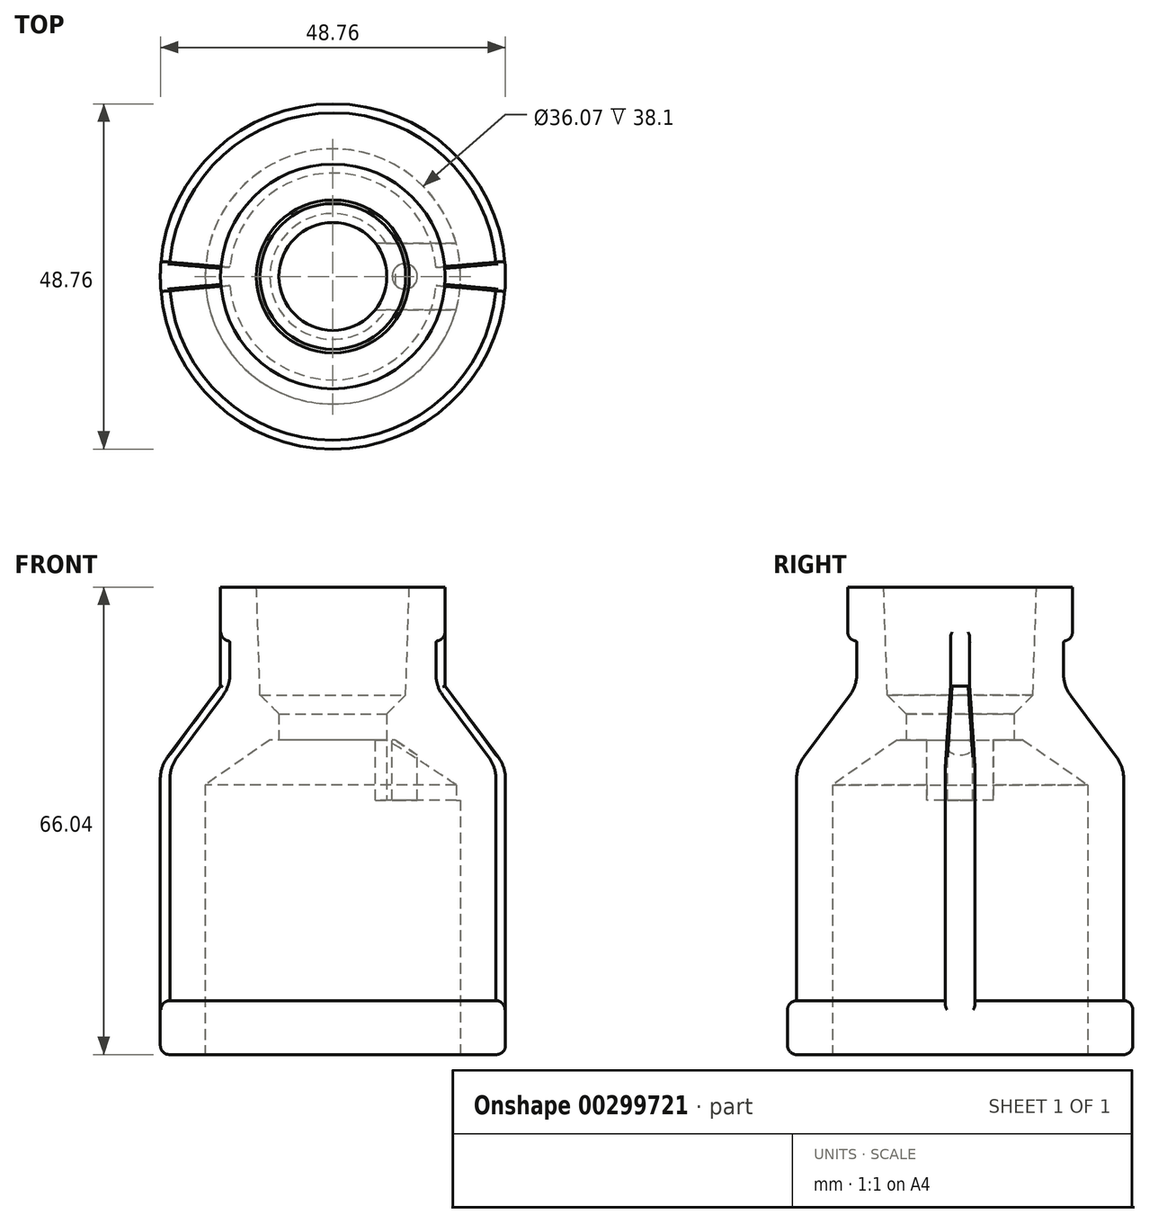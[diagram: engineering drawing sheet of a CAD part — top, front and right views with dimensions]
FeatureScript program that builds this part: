
annotation { "Feature Type Name" : "Feature", "Feature Type Description" : "" }
export const myFeature = defineFeature(function(context is Context, id is Id, definition is map)
    precondition{}
    {
        {
            var Q0;
            Q0=qCreatedBy(makeId("Front.planeOp"),FACE);
            var sketch = newSketch(context, id + "F0", { "sketchPlane" : qUnion([Q0])});
            skLineSegment(sketch, "E0", {"start": v(0, 1.67) * mm, "end": v(0, 16.9) * mm});
            skLineSegment(sketch, "E1", {"start": v(0, 16.9) * mm, "end": v(10.8, 16.9) * mm});
            skLineSegment(sketch, "E2", {"start": v(10.8, 16.9) * mm, "end": v(15.88, 16.9) * mm});
            skLineSegment(sketch, "E3", {"start": v(15.88, 16.9) * mm, "end": v(15.88, 9.29) * mm});
            skLineSegment(sketch, "E4", {"start": v(15.88, 9.29) * mm, "end": v(14.6, 9.29) * mm});
            skLineSegment(sketch, "E5", {"start": v(0, 1.67) * mm, "end": v(10.29, 1.67) * mm});
            skLineSegment(sketch, "E6", {"start": v(10.29, 1.67) * mm, "end": v(10.8, 16.9) * mm});
            skLineSegment(sketch, "E7", {"start": v(0, 1.67) * mm, "end": v(0, -4.68) * mm});
            skLineSegment(sketch, "E8", {"start": v(0, -4.68) * mm, "end": v(8.9, -4.68) * mm});
            skLineSegment(sketch, "E9", {"start": v(0, -4.68) * mm, "end": v(0, -11.03) * mm});
            skLineSegment(sketch, "E10", {"start": v(0, -11.03) * mm, "end": v(18.03, -11.03) * mm});
            skLineSegment(sketch, "E11", {"start": v(18.03, -11.03) * mm, "end": v(18.03, -49.13) * mm});
            skLineSegment(sketch, "E12", {"start": v(8.89, -4.68) * mm, "end": v(18.03, -11.03) * mm});
            skLineSegment(sketch, "E13", {"start": v(18.03, -49.13) * mm, "end": v(24.38, -49.13) * mm});
            skLineSegment(sketch, "E14", {"start": v(24.38, -49.13) * mm, "end": v(24.38, -41.51) * mm});
            skLineSegment(sketch, "E15", {"start": v(24.38, -41.51) * mm, "end": v(23.11, -41.51) * mm});
            skLineSegment(sketch, "E16", {"start": v(23.11, -41.51) * mm, "end": v(23.11, -8.5) * mm});
            skLineSegment(sketch, "E17", {"start": v(14.6, 9.29) * mm, "end": v(14.6, 2.94) * mm});
            skLineSegment(sketch, "E18", {"start": v(14.6, 2.94) * mm, "end": v(23.11, -8.5) * mm});
            skLineSegment(sketch, "E19", {"start": v(0, 1.67) * mm, "end": v(0, -8.62) * mm});
            skLineSegment(sketch, "E20", {"start": v(0, -4.68) * mm, "end": v(7.62, -4.68) * mm});
            skLineSegment(sketch, "E21", {"start": v(7.62, -4.68) * mm, "end": v(7.62, -1) * mm});
            skLineSegment(sketch, "E22", {"start": v(10.29, 1.67) * mm, "end": v(7.62, -1) * mm});
            skLineSegment(sketch, "E23", {"start": v(15.88, 9.29) * mm, "end": v(15.88, 2.94) * mm});
            skLineSegment(sketch, "E24", {"start": v(15.88, 2.94) * mm, "end": v(24.38, -8.5) * mm});
            skLineSegment(sketch, "E25", {"start": v(24.38, -8.5) * mm, "end": v(24.38, -41.51) * mm});
            skLineSegment(sketch, "E26", {"start": v(14.6, 9.29) * mm, "end": v(14.6, 12.15) * mm});
            skLineSegment(sketch, "E27", {"start": v(14.6, 12.15) * mm, "end": v(15.88, 12.1) * mm});
            skLineSegment(sketch, "E28", {"start": v(24.38, -41.51) * mm, "end": v(24.38, -43.7) * mm});
            skLineSegment(sketch, "E29", {"start": v(24.38, -43.7) * mm, "end": v(23.11, -43.7) * mm});
            skLineSegment(sketch, "E30", {"start": v(23.11, -43.7) * mm, "end": v(23.11, -41.51) * mm});
            skLineSegment(sketch, "E31.MirrorCS", {"start": v(-24.38, -8.5) * mm, "end": v(-24.38, -41.51) * mm});
            skLineSegment(sketch, "E32.MirrorCS", {"start": v(-15.87, 2.94) * mm, "end": v(-24.38, -8.5) * mm});
            skLineSegment(sketch, "E33.MirrorCS", {"start": v(-14.6, 2.94) * mm, "end": v(-23.11, -8.5) * mm});
            skLineSegment(sketch, "E34.MirrorCS", {"start": v(-23.11, -41.51) * mm, "end": v(-23.11, -8.5) * mm});
            skLineSegment(sketch, "E35.MirrorCS", {"start": v(-24.38, -41.51) * mm, "end": v(-24.38, -43.7) * mm});
            skLineSegment(sketch, "E36.MirrorCS", {"start": v(-23.11, -43.7) * mm, "end": v(-23.11, -41.51) * mm});
            skLineSegment(sketch, "E37.MirrorCS", {"start": v(-24.38, -43.7) * mm, "end": v(-23.11, -43.7) * mm});
            skLineSegment(sketch, "E38.MirrorCS", {"start": v(-14.6, 12.15) * mm, "end": v(-15.88, 12.1) * mm});
            skLineSegment(sketch, "E39.MirrorCS", {"start": v(-14.6, 9.29) * mm, "end": v(-14.6, 12.15) * mm});
            skLineSegment(sketch, "E40.MirrorCS", {"start": v(-15.88, 16.9) * mm, "end": v(-15.88, 9.29) * mm});
            skLineSegment(sketch, "E41.MirrorCS", {"start": v(-14.6, 9.29) * mm, "end": v(-14.6, 2.94) * mm});
            skLineSegment(sketch, "E42.MirrorCS", {"start": v(-15.88, 9.29) * mm, "end": v(-15.88, 2.94) * mm});
            skSolve(sketch);
        }
        {
            var Q0;
            Q0=makeQuery(id+"F0.imprint","IMPRINT",FACE,{"disambiguationData":[TD([[makeQuery(id+"F0.imprint","IMPRINT",EDGE,{"derivedFrom":sQuery(id+"F0.wireOp",EDGE,"E2")}),-1.0]])]});
            var Q1;
            Q1=makeQuery(id+"F0.imprint","IMPRINT",FACE,{"disambiguationData":[TD([[makeQuery(id+"F0.imprint","IMPRINT",EDGE,{"derivedFrom":sQuery(id+"F0.wireOp",EDGE,"E15")}),1.0]])]});
            var Q2;
            {var subQ0=sQuery(id+"F0.wireOp",EDGE,"E4");Q2=makeQuery(id+"F0.imprint","IMPRINT",FACE,{"disambiguationData":[TD([[makeQuery(id+"F0.imprint","IMPRINT",EDGE,{"derivedFrom":subQ0}),-1.0]])]});}
            var Q3;
            Q3=sQuery(id+"F0.wireOp",EDGE,"E0");
            revolve(context, id + "F1", {"entities" : qUnion([Q0, Q1, Q2]), "axis" : qUnion([Q3]), "revolveType" : RevolveType.FULL});
        }
        {
            var Q0;
            Q0=makeQuery(id+"F1.opRevolve","SWEPT_EDGE",EDGE,{"disambiguationData":[OSD([sQuery(id+"F0.wireOp",EDGE,"E3"),sQuery(id+"F0.wireOp",EDGE,"E4")])]});
            var Q1;
            Q1=makeQuery(id+"F1.opRevolve","SWEPT_EDGE",EDGE,{"disambiguationData":[OSD([sQuery(id+"F0.wireOp",EDGE,"E14"),sQuery(id+"F0.wireOp",EDGE,"E15")])]});
            var Q2;
            Q2=makeQuery(id+"F1.opRevolve","SWEPT_EDGE",EDGE,{"disambiguationData":[OSD([sQuery(id+"F0.wireOp",EDGE,"E13"),sQuery(id+"F0.wireOp",EDGE,"E14")])]});
            fillet(context, id + "F2", {"entities" : qUnion([Q0, Q1, Q2]), "radius" : 1.27 * mm, "tangentPropagation" : true, "allowEdgeOverflow" : false});
        }
        {
            var Q0;
            Q0=makeQuery(id+"F1.opRevolve","SWEPT_EDGE",EDGE,{"disambiguationData":[OSD([sQuery(id+"F0.wireOp",EDGE,"E17"),sQuery(id+"F0.wireOp",EDGE,"E18")])]});
            var Q1;
            Q1=makeQuery(id+"F1.opRevolve","SWEPT_EDGE",EDGE,{"disambiguationData":[OSD([sQuery(id+"F0.wireOp",EDGE,"E16"),sQuery(id+"F0.wireOp",EDGE,"E18")])]});
            fillet(context, id + "F3", {"entities" : qUnion([Q0, Q1]), "radius" : 5.08 * mm, "tangentPropagation" : true, "allowEdgeOverflow" : false});
        }
        {
            var Q0;
            Q0=makeQuery(id+"F0.imprint","IMPRINT",FACE,{"disambiguationData":[TD([[makeQuery(id+"F0.imprint","IMPRINT",EDGE,{"derivedFrom":sQuery(id+"F0.wireOp",EDGE,"E4")}),1.0]])]});
            var Q1;
            Q1=makeQuery(id+"F0.imprint","IMPRINT",FACE,{"disambiguationData":[TD([[makeQuery(id+"F0.imprint","IMPRINT",EDGE,{"derivedFrom":sQuery(id+"F0.wireOp",EDGE,"E15")}),1.0]])]});
            var Q2;
            {var subQ0=sQuery(id+"F0.wireOp",EDGE,"E4");Q2=makeQuery(id+"F0.imprint","IMPRINT",FACE,{"disambiguationData":[TD([[makeQuery(id+"F0.imprint","IMPRINT",EDGE,{"derivedFrom":subQ0}),-1.0]])]});}
            var Q3;
            Q3=sQuery(id+"F0.wireOp",EDGE,"E0");
            revolve(context, id + "F4", {"operationType" : NewBodyOperationType.ADD, "entities" : qUnion([Q0, Q1, Q2]), "axis" : qUnion([Q3]), "revolveType" : RevolveType.SYMMETRIC, "angle" : 10 * degree});
        }
        {
            var Q0;
            Q0=makeQuery(id+"F4.opRevolve","SWEPT_EDGE",EDGE,{"disambiguationData":[OSD([sQuery(id+"F0.wireOp",EDGE,"E16"),sQuery(id+"F0.wireOp",EDGE,"E18")])]});
            var Q1;
            Q1=makeQuery(id+"F4.opRevolve","SWEPT_EDGE",EDGE,{"disambiguationData":[OSD([sQuery(id+"F0.wireOp",EDGE,"E24"),sQuery(id+"F0.wireOp",EDGE,"E25")])]});
            fillet(context, id + "F5", {"entities" : qUnion([Q0, Q1]), "radius" : 5.08 * mm, "tangentPropagation" : true, "allowEdgeOverflow" : false});
        }
        {
            var Q0;
            Q0=makeQuery(id+"F0.imprint","IMPRINT",FACE,{"disambiguationData":[TD([[makeQuery(id+"F0.imprint","IMPRINT",EDGE,{"derivedFrom":sQuery(id+"F0.wireOp",EDGE,"E31.MirrorCS")}),1.0]])]});
            var Q1;
            Q1=sQuery(id+"F0.wireOp",EDGE,"E0");
            revolve(context, id + "F6", {"operationType" : NewBodyOperationType.ADD, "entities" : qUnion([Q0]), "axis" : qUnion([Q1]), "revolveType" : RevolveType.SYMMETRIC, "angle" : 10 * degree});
        }
        {
            var Q0;
            Q0=makeQuery(id+"F6.opRevolve","SWEPT_EDGE",EDGE,{"disambiguationData":[OSD([sQuery(id+"F0.wireOp",EDGE,"E33.MirrorCS"),sQuery(id+"F0.wireOp",EDGE,"E34.MirrorCS")])]});
            var Q1;
            Q1=makeQuery(id+"F6.opRevolve","SWEPT_EDGE",EDGE,{"disambiguationData":[OSD([sQuery(id+"F0.wireOp",EDGE,"E31.MirrorCS"),sQuery(id+"F0.wireOp",EDGE,"E32.MirrorCS")])]});
            fillet(context, id + "F7", {"entities" : qUnion([Q0, Q1]), "radius" : 5.08 * mm, "tangentPropagation" : true, "allowEdgeOverflow" : false});
        }
        {
            var Q0;
            Q0=makeQuery(id+"F4.opRevolve","CAP_EDGE",EDGE,{"disambiguationData":[OSD([sQuery(id+"F0.wireOp",EDGE,"E24")])],"isStart":false});
            var Q1;
            Q1=makeQuery(id+"F4.opRevolve","CAP_EDGE",EDGE,{"disambiguationData":[OSD([sQuery(id+"F0.wireOp",EDGE,"E24")])],"isStart":true});
            var Q2;
            Q2=makeQuery(id+"F4.opRevolve","CAP_EDGE",EDGE,{"disambiguationData":[OSD([sQuery(id+"F0.wireOp",EDGE,"E3"),sQuery(id+"F0.wireOp",EDGE,"E23")])],"isStart":false});
            var Q3;
            Q3=makeQuery(id+"F4.opRevolve","CAP_EDGE",EDGE,{"disambiguationData":[OSD([sQuery(id+"F0.wireOp",EDGE,"E3"),sQuery(id+"F0.wireOp",EDGE,"E23")])],"isStart":true});
            var Q4;
            Q4=makeQuery(id+"F6.opRevolve","CAP_EDGE",EDGE,{"disambiguationData":[OSD([sQuery(id+"F0.wireOp",EDGE,"E32.MirrorCS")])],"isStart":true});
            var Q5;
            Q5=makeQuery(id+"F6.opRevolve","CAP_EDGE",EDGE,{"disambiguationData":[OSD([sQuery(id+"F0.wireOp",EDGE,"E40.MirrorCS"),sQuery(id+"F0.wireOp",EDGE,"E42.MirrorCS")])],"isStart":true});
            var Q6;
            Q6=makeQuery(id+"F6.opRevolve","CAP_EDGE",EDGE,{"disambiguationData":[OSD([sQuery(id+"F0.wireOp",EDGE,"E40.MirrorCS"),sQuery(id+"F0.wireOp",EDGE,"E42.MirrorCS")])],"isStart":false});
            var Q7;
            Q7=makeQuery(id+"F6.opRevolve","CAP_EDGE",EDGE,{"disambiguationData":[OSD([sQuery(id+"F0.wireOp",EDGE,"E32.MirrorCS")])],"isStart":false});
            var Q8;
            Q8=makeQuery(id+"F6.opRevolve","CAP_EDGE",EDGE,{"disambiguationData":[OSD([sQuery(id+"F0.wireOp",EDGE,"E39.MirrorCS"),sQuery(id+"F0.wireOp",EDGE,"E41.MirrorCS")])],"isStart":true});
            var Q9;
            Q9=makeQuery(id+"F6.opRevolve","CAP_EDGE",EDGE,{"disambiguationData":[OSD([sQuery(id+"F0.wireOp",EDGE,"E39.MirrorCS"),sQuery(id+"F0.wireOp",EDGE,"E41.MirrorCS")])],"isStart":false});
            var Q10;
            {var subQ0=sQuery(id+"F0.wireOp",EDGE,"E17");var subQ1=makeQuery(id+"F1.opRevolve","SWEPT_FACE",FACE,{"disambiguationData":[OSD([subQ0])]});var subQ2=sQuery(id+"F0.wireOp",EDGE,"E23");var subQ3=sQuery(id+"F0.wireOp",EDGE,"E4");var subQ4=sQuery(id+"F0.wireOp",EDGE,"E3");Q10=makeQuery(id+"F6.boolean.opBoolean","SPLIT",EDGE,{"disambiguationData":[TD([makeQuery(id+"F4.opRevolve","CAP_FACE",FACE,{"disambiguationData":[OSD([subQ4,sQuery(id+"F0.wireOp",EDGE,"E16"),subQ0,sQuery(id+"F0.wireOp",EDGE,"E18"),subQ2,sQuery(id+"F0.wireOp",EDGE,"E24"),sQuery(id+"F0.wireOp",EDGE,"E25"),sQuery(id+"F0.wireOp",EDGE,"E26"),sQuery(id+"F0.wireOp",EDGE,"E27"),sQuery(id+"F0.wireOp",EDGE,"E28"),sQuery(id+"F0.wireOp",EDGE,"E29"),sQuery(id+"F0.wireOp",EDGE,"E30")])],"isStart":true})])],"derivedFrom":makeQuery(id+"F2.opFillet","BLEND_EDGE",EDGE,{"blendedFrom":[makeQuery(id+"F1.opRevolve","SWEPT_EDGE",EDGE,{"disambiguationData":[OSD([subQ4,subQ3,subQ2])]}),subQ1],"blendedInto":[subQ1]})});}
            var Q11;
            {var subQ0=sQuery(id+"F0.wireOp",EDGE,"E17");var subQ1=makeQuery(id+"F1.opRevolve","SWEPT_FACE",FACE,{"disambiguationData":[OSD([subQ0])]});var subQ2=sQuery(id+"F0.wireOp",EDGE,"E23");var subQ3=sQuery(id+"F0.wireOp",EDGE,"E4");var subQ4=sQuery(id+"F0.wireOp",EDGE,"E3");Q11=makeQuery(id+"F6.boolean.opBoolean","SPLIT",EDGE,{"disambiguationData":[TD([makeQuery(id+"F4.opRevolve","CAP_FACE",FACE,{"disambiguationData":[OSD([subQ4,sQuery(id+"F0.wireOp",EDGE,"E16"),subQ0,sQuery(id+"F0.wireOp",EDGE,"E18"),subQ2,sQuery(id+"F0.wireOp",EDGE,"E24"),sQuery(id+"F0.wireOp",EDGE,"E25"),sQuery(id+"F0.wireOp",EDGE,"E26"),sQuery(id+"F0.wireOp",EDGE,"E27"),sQuery(id+"F0.wireOp",EDGE,"E28"),sQuery(id+"F0.wireOp",EDGE,"E29"),sQuery(id+"F0.wireOp",EDGE,"E30")])],"isStart":false})])],"derivedFrom":makeQuery(id+"F2.opFillet","BLEND_EDGE",EDGE,{"blendedFrom":[makeQuery(id+"F1.opRevolve","SWEPT_EDGE",EDGE,{"disambiguationData":[OSD([subQ4,subQ3,subQ2])]}),subQ1],"blendedInto":[subQ1]})});}
            var Q12;
            Q12=makeQuery(id+"F4.opRevolve","CAP_EDGE",EDGE,{"disambiguationData":[OSD([sQuery(id+"F0.wireOp",EDGE,"E17"),sQuery(id+"F0.wireOp",EDGE,"E26")])],"isStart":false});
            var Q13;
            Q13=makeQuery(id+"F4.opRevolve","CAP_EDGE",EDGE,{"disambiguationData":[OSD([sQuery(id+"F0.wireOp",EDGE,"E17"),sQuery(id+"F0.wireOp",EDGE,"E26")])],"isStart":true});
            var Q14;
            {var subQ0=sQuery(id+"F0.wireOp",EDGE,"E15");var subQ1=sQuery(id+"F0.wireOp",EDGE,"E16");var subQ2=sQuery(id+"F0.wireOp",EDGE,"E30");Q14=makeQuery(id+"F6.boolean.opBoolean","SPLIT",EDGE,{"disambiguationData":[TD([makeQuery(id+"F4.opRevolve","CAP_FACE",FACE,{"disambiguationData":[OSD([sQuery(id+"F0.wireOp",EDGE,"E3"),subQ1,sQuery(id+"F0.wireOp",EDGE,"E17"),sQuery(id+"F0.wireOp",EDGE,"E18"),sQuery(id+"F0.wireOp",EDGE,"E23"),sQuery(id+"F0.wireOp",EDGE,"E24"),sQuery(id+"F0.wireOp",EDGE,"E25"),sQuery(id+"F0.wireOp",EDGE,"E26"),sQuery(id+"F0.wireOp",EDGE,"E27"),sQuery(id+"F0.wireOp",EDGE,"E28"),sQuery(id+"F0.wireOp",EDGE,"E29"),subQ2])],"isStart":true})])],"derivedFrom":makeQuery(id+"F1.opRevolve","SWEPT_EDGE",EDGE,{"disambiguationData":[OSD([subQ0,subQ1,subQ2])]})});}
            var Q15;
            {var subQ0=sQuery(id+"F0.wireOp",EDGE,"E28");var subQ1=sQuery(id+"F0.wireOp",EDGE,"E25");var subQ2=sQuery(id+"F0.wireOp",EDGE,"E15");Q15=makeQuery(id+"F6.boolean.opBoolean","SPLIT",EDGE,{"disambiguationData":[TD([makeQuery(id+"F4.opRevolve","CAP_FACE",FACE,{"disambiguationData":[OSD([sQuery(id+"F0.wireOp",EDGE,"E3"),sQuery(id+"F0.wireOp",EDGE,"E16"),sQuery(id+"F0.wireOp",EDGE,"E17"),sQuery(id+"F0.wireOp",EDGE,"E18"),sQuery(id+"F0.wireOp",EDGE,"E23"),sQuery(id+"F0.wireOp",EDGE,"E24"),subQ1,sQuery(id+"F0.wireOp",EDGE,"E26"),sQuery(id+"F0.wireOp",EDGE,"E27"),subQ0,sQuery(id+"F0.wireOp",EDGE,"E29"),sQuery(id+"F0.wireOp",EDGE,"E30")])],"isStart":true})])],"derivedFrom":makeQuery(id+"F1.opRevolve","SWEPT_EDGE",EDGE,{"disambiguationData":[OSD([subQ2,subQ1,subQ0])]})});}
            var Q16;
            {var subQ0=sQuery(id+"F0.wireOp",EDGE,"E15");var subQ1=sQuery(id+"F0.wireOp",EDGE,"E30");var subQ2=sQuery(id+"F0.wireOp",EDGE,"E16");Q16=makeQuery(id+"F6.boolean.opBoolean","SPLIT",EDGE,{"disambiguationData":[TD([makeQuery(id+"F4.opRevolve","CAP_FACE",FACE,{"disambiguationData":[OSD([sQuery(id+"F0.wireOp",EDGE,"E3"),subQ2,sQuery(id+"F0.wireOp",EDGE,"E17"),sQuery(id+"F0.wireOp",EDGE,"E18"),sQuery(id+"F0.wireOp",EDGE,"E23"),sQuery(id+"F0.wireOp",EDGE,"E24"),sQuery(id+"F0.wireOp",EDGE,"E25"),sQuery(id+"F0.wireOp",EDGE,"E26"),sQuery(id+"F0.wireOp",EDGE,"E27"),sQuery(id+"F0.wireOp",EDGE,"E28"),sQuery(id+"F0.wireOp",EDGE,"E29"),subQ1])],"isStart":false})])],"derivedFrom":makeQuery(id+"F1.opRevolve","SWEPT_EDGE",EDGE,{"disambiguationData":[OSD([subQ0,subQ2,subQ1])]})});}
            var Q17;
            {var subQ0=sQuery(id+"F0.wireOp",EDGE,"E28");var subQ1=sQuery(id+"F0.wireOp",EDGE,"E25");var subQ4=sQuery(id+"F0.wireOp",EDGE,"E15");Q17=makeQuery(id+"F6.boolean.opBoolean","SPLIT",EDGE,{"disambiguationData":[TD([makeQuery(id+"F4.opRevolve","CAP_FACE",FACE,{"disambiguationData":[OSD([sQuery(id+"F0.wireOp",EDGE,"E3"),sQuery(id+"F0.wireOp",EDGE,"E16"),sQuery(id+"F0.wireOp",EDGE,"E17"),sQuery(id+"F0.wireOp",EDGE,"E18"),sQuery(id+"F0.wireOp",EDGE,"E23"),sQuery(id+"F0.wireOp",EDGE,"E24"),subQ1,sQuery(id+"F0.wireOp",EDGE,"E26"),sQuery(id+"F0.wireOp",EDGE,"E27"),subQ0,sQuery(id+"F0.wireOp",EDGE,"E29"),sQuery(id+"F0.wireOp",EDGE,"E30")])],"isStart":false})])],"derivedFrom":makeQuery(id+"F1.opRevolve","SWEPT_EDGE",EDGE,{"disambiguationData":[OSD([subQ4,subQ1,subQ0])]})});}
            fillet(context, id + "F8", {"entities" : qUnion([Q0, Q1, Q2, Q3, Q4, Q5, Q6, Q7, Q8, Q9, Q10, Q11, Q12, Q13, Q14, Q15, Q16, Q17]), "radius" : 0.25 * mm, "tangentPropagation" : true, "allowEdgeOverflow" : false});
        }
        {
            var Q0;
            Q0=makeQuery(id+"F1.opRevolve","SWEPT_FACE",FACE,{"disambiguationData":[OSD([sQuery(id+"F0.wireOp",EDGE,"E8")])]});
            var sketch = newSketch(context, id + "F9", { "sketchPlane" : qUnion([Q0])});
            skLineSegment(sketch, "E43", {"start": v(0, 0) * mm, "end": v(18.03, 0) * mm});
            skLineSegment(sketch, "E44", {"start": v(18.03, 0) * mm, "end": v(18.03, -4.7) * mm});
            skLineSegment(sketch, "E45", {"start": v(18.03, -4.7) * mm, "end": v(5.08, -4.7) * mm});
            skLineSegment(sketch, "E46", {"start": v(5.08, -4.7) * mm, "end": v(5.08, 4.7) * mm});
            skLineSegment(sketch, "E47", {"start": v(5.08, 4.7) * mm, "end": v(18.03, 4.7) * mm});
            skLineSegment(sketch, "E48", {"start": v(18.03, 4.7) * mm, "end": v(18.03, 0) * mm});
            skLineSegment(sketch, "E49", {"start": v(18.03, 0) * mm, "end": v(10.16, 0) * mm});
            skCircle(sketch, "E50", {"center": v(10.16, 0) * mm, "radius": 1.78 * mm});
            skCircle(sketch, "E51", {"center": v(0, 0) * mm, "radius": 7.62 * mm});
            skSolve(sketch);
        }
        {
            var Q0;
            {var subQ0=sQuery(id+"F9.wireOp",EDGE,"E51");var subQ1=sQuery(id+"F9.wireOp",EDGE,"E43");var subQ2=makeQuery(id+"F9.imprint","INTERSECT",VERTEX,{"derivedFrom":[subQ1,subQ0]});Q0=makeQuery(id+"F9.imprint","IMPRINT",FACE,{"disambiguationData":[TD([[makeQuery(id+"F9.imprint","IMPRINT",EDGE,{"disambiguationData":[TD([[subQ2,-1.0]])],"derivedFrom":subQ1}),1.0]])]});}
            var Q1;
            {var subQ0=sQuery(id+"F9.wireOp",EDGE,"E51");var subQ1=sQuery(id+"F9.wireOp",EDGE,"E43");var subQ2=makeQuery(id+"F9.imprint","INTERSECT",VERTEX,{"derivedFrom":[subQ1,subQ0]});Q1=makeQuery(id+"F9.imprint","IMPRINT",FACE,{"disambiguationData":[TD([[makeQuery(id+"F9.imprint","IMPRINT",EDGE,{"disambiguationData":[TD([[subQ2,-1.0]])],"derivedFrom":subQ1}),-1.0]])]});}
            var Q2;
            {var subQ6=sQuery(id+"F9.wireOp",EDGE,"E44");Q2=makeQuery(id+"F9.imprint","IMPRINT",FACE,{"disambiguationData":[TD([[makeQuery(id+"F9.imprint","IMPRINT",EDGE,{"derivedFrom":subQ6}),-1.0]])]});}
            var Q3;
            {var subQ5=sQuery(id+"F9.wireOp",EDGE,"E48");Q3=makeQuery(id+"F9.imprint","IMPRINT",FACE,{"disambiguationData":[TD([[makeQuery(id+"F9.imprint","IMPRINT",EDGE,{"derivedFrom":subQ5}),-1.0]])]});}
            extrude(context, id + "F10", {"entities" : qUnion([Q0, Q1, Q2, Q3]), "operationType" : NewBodyOperationType.ADD, "depth" : 8.5 * mm});
        }
    });
